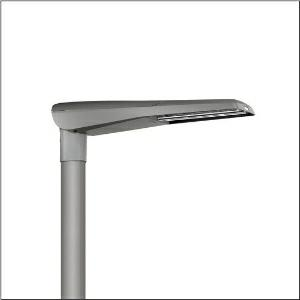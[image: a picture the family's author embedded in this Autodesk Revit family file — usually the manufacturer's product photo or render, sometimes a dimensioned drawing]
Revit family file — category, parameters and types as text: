
# Revit family: streetlight_sl_11_iq_mini___st1_2a_5xc2ac1g08ge_ba73
name_source: partatom
category: Lighting Fixtures
units: mm (PartAtom-declared; Revit-internal decimal feet)

## family parameters
Cut with Voids When Loaded = No
Host = Face
Light Source = No
Part Type = Normal
Room Calculation Point = No
Round Connector Dimension = Use Diameter
Shared = No

## types (1)
- --- (1 x LED, 3040 lm, 25.3 W, 2200K)
    Apparent Load = 25 VA
    CIE Flux Codes = 32 70 96 100 100
    Color Rendering = 70
    Color Temperature = 2200K
    Default Elevation = 1800 mm
    Description = Streetlight SL 11 iQ mini, mast luminaire, primary light control with 3 zone facetted reflector, of plastic, silver coated, highly specular, primary optical cover: cover, of PMMA, transparent, light distribution: ST1.2a, light emission: direct distribution, primary light characteristic: asymmetric, installation type: post-top, side-entry, LED, High Power LED, rated luminous flux: 3.570lm, luminous efficacy: 143lm/W, light colour: 722/727/730/740, colour temperature: 2200/2700/3000/4000K, control gear: iQ Street-Remote/DALI, control: pre-setting: linear dimming characteristic, Street-Remote, Auto-Match, Temp-Guard, Lumen-Switch, Night-Set, Smart-Wire, Light-Fading, Desk-Remote (wireless, voltage-free reading and setting of iQ features in the workshop via application-optimized NFC function/RFID function), optimised constant luminous flux control (CLO 2.0), with cable H07RN-F 5x 1.5mm², mains connection: 230..240V, AC, 50/60Hz, connection cable pre-assembled, cable length: 6,5m, start of lifetime: 25W, end of service life: 26W, reduction: 13W, luminaire housing, of diecast aluminium, powder-coated, Siteco® metallic grey (DB 702S), please order mast flange separately, inclination adjustable without tools: 0°, 5°, 10°, 15° (post-top) | 0°, -5°, -10°, -15° (side-entry), sealing non-destructively replaceable, multi-level sealing system, length: 736mm, width: 174mm, height: 116mm, mast flange for spigot size: 42mm (side-entry): 5XC10008XM4, 60/48mm (side-entry/post-top): 5XC10108XM2, 76/60mm (side-entry/post-top): 5XC10108XM1, mounting height: 4..8m, equipment: standard, protection rating (complete): IP66, insulation class (complete): insulation class II (safety insulation), certification: CE, ENEC, VDE, impact resistance: IK09, permissible operating ambient temperature for outdoor applications: -25..+50°C, standard-compliant lighting for roads and squares, Environmental Product Declaration (EPD) tested and certified by an independent institute, packaging unit: 1 piece

Light Distribution: ST1.2a
    Height = 116 mm
    Lamp = 1 x LED
    Lamp Light Flux = 3040 lm
    Lamp Power = 25.3 W
    Lamp count = 1
    Length = 736 mm
    Luminous efficacy = 120 lm/W
    Manufacturer = Siteco
    ModVariant = No
    Model = 5XC2AC1G08GE
    Number of Poles = 1
    OnlyDefault = Yes
    Power Factor = 1
    Product Name = Streetlight SL 11 iQ mini | ST1.2a
    Product group = mast luminaire | pylon top
    ProductGroupID = 6100
    Protection Class = Protection class II
    Protection Degree = IP 66
    RLX_Detail_Level = 1
    RLX_Emergency_Light_Flux = 0 lm
    RLX_Emergency_Type = 0
    RLX_Emergency_Type_DB = No
    RlxData = <blob elided: 53277 chars, md5=ea57e9b7>
    Socket = socket
    Standby Power = 0 W
    System Light Flux = 3040 lm
    System Power = 25 W
    Type Comments = individual setting: luminous flux: 100 % | dim-lin: 254 | 351 mA
    Type Image = l_1003508.jpg
    URL = http://relux.com
    VarID = @adj_031872
    Voltage = 0 V
    Weight = 0.00 kg
    Width = 174 mm

## geometry (parser evidence)
native form markers: Blend x4, Sweep x9
no freeform markers — native parametric forms only
